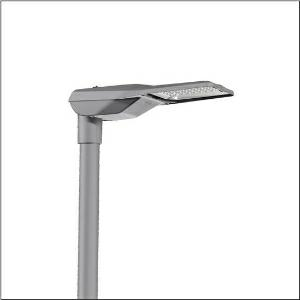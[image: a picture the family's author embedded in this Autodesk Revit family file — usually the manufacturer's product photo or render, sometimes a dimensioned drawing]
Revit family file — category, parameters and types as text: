
# Revit family: streetlight_sl_21_mini___st0_5a_5xe2b33s08gb_907c
name_source: partatom
category: Lighting Fixtures
units: mm (PartAtom-declared; Revit-internal decimal feet)

## family parameters
Cut with Voids When Loaded = No
Host = Face
Light Source = No
Part Type = Normal
Room Calculation Point = No
Round Connector Dimension = Use Diameter
Shared = No

## types (1)
- --- (1 x LED, 5940 lm, 40.4 W, 3000K)
    Apparent Load = 40 VA
    CIE Flux Codes = 41 75 97 100 100
    Color Rendering = 70
    Color Temperature = 3000K
    Default Elevation = 1800 mm
    Description = Streetlight SL 21 mini, mast luminaire, primary light control with lens, of PMMA, primary optical cover: cover, of toughened safety glass, transparent, light distribution: ST0.5a, light emission: direct distribution, primary light characteristic: asymmetric, installation type: side-entry, post-top, LED, High Power LED, rated luminous flux: 5.940lm, luminous efficacy: 147lm/W, light colour: 730, colour temperature: 3000K, control gear: D4i, control: overheat protection, constant luminous flux control, time-dependent luminous flux control, flexible luminous flux parameterisation, pre-setting: logarithmic dimming characteristic, mains connection: 220..240V, AC, 50/60Hz, start of lifetime: 40W, end of service life: 41W, reduction: 19W, luminaire housing, of diecast aluminium, powder-coated, Siteco® metallic grey (DB 702S), corrosivity category C5 mid according to DIN EN ISO 12944, please order mast flange separately, inclination adjustable: 0°, 5°, 10°, 15°, sealing non-destructively replaceable, multi-level sealing system, length: 628mm, width: 235mm, height: 110mm, mast flange for spigot size: 42mm (side-entry): 5XC10008XM4, 60/48mm (side-entry/post-top): 5XC10108XM2, 76/60mm (side-entry/post-top): 5XC10108XM1, mounting height: 4..8m, Smart Interface above, protection rating (complete): IP66, insulation class (complete): insulation class II (safety insulation), certification: CE, ENEC, ENEC+, VDE, impact resistance: IK10, permissible operating ambient temperature for outdoor applications: -40..+50°C, standard-compliant lighting for roads and squares, packaging unit: 1 piece

Light Distribution: ST0.5a
    Height = 110 mm
    Lamp = 1 x LED
    Lamp Light Flux = 5940 lm
    Lamp Power = 40.4 W
    Lamp count = 1
    Length = 625 mm
    Luminous efficacy = 147 lm/W
    Manufacturer = Siteco
    ModVariant = No
    Model = 5XE2B33S08GB
    Number of Poles = 1
    OnlyDefault = Yes
    Power Factor = 1
    Product Name = Streetlight SL 21 mini | ST0.5a
    Product group = mast luminaire | pylon top
    ProductGroupID = 6100
    Protection Class = Protection class II
    Protection Degree = IP 66
    RLX_Detail_Level = 1
    RLX_Emergency_Light_Flux = 0 lm
    RLX_Emergency_Type = 0
    RLX_Emergency_Type_DB = No
    RlxData = <blob elided: 37121 chars, md5=6acd1533>
    Socket = socket
    Standby Power = 0 W
    System Light Flux = 5940 lm
    System Power = 40 W
    Type Comments = factory setting: luminous flux: 100 % | dim-lin: 254 | 812 mA
    Type Image = l_1003515.jpg
    URL = http://relux.com
    VarID = @adj_212561
    Voltage = 0 V
    Weight = 0.00 kg
    Width = 234 mm

## geometry (parser evidence)
native form markers: Blend x4, Sweep x12
no freeform markers — native parametric forms only
